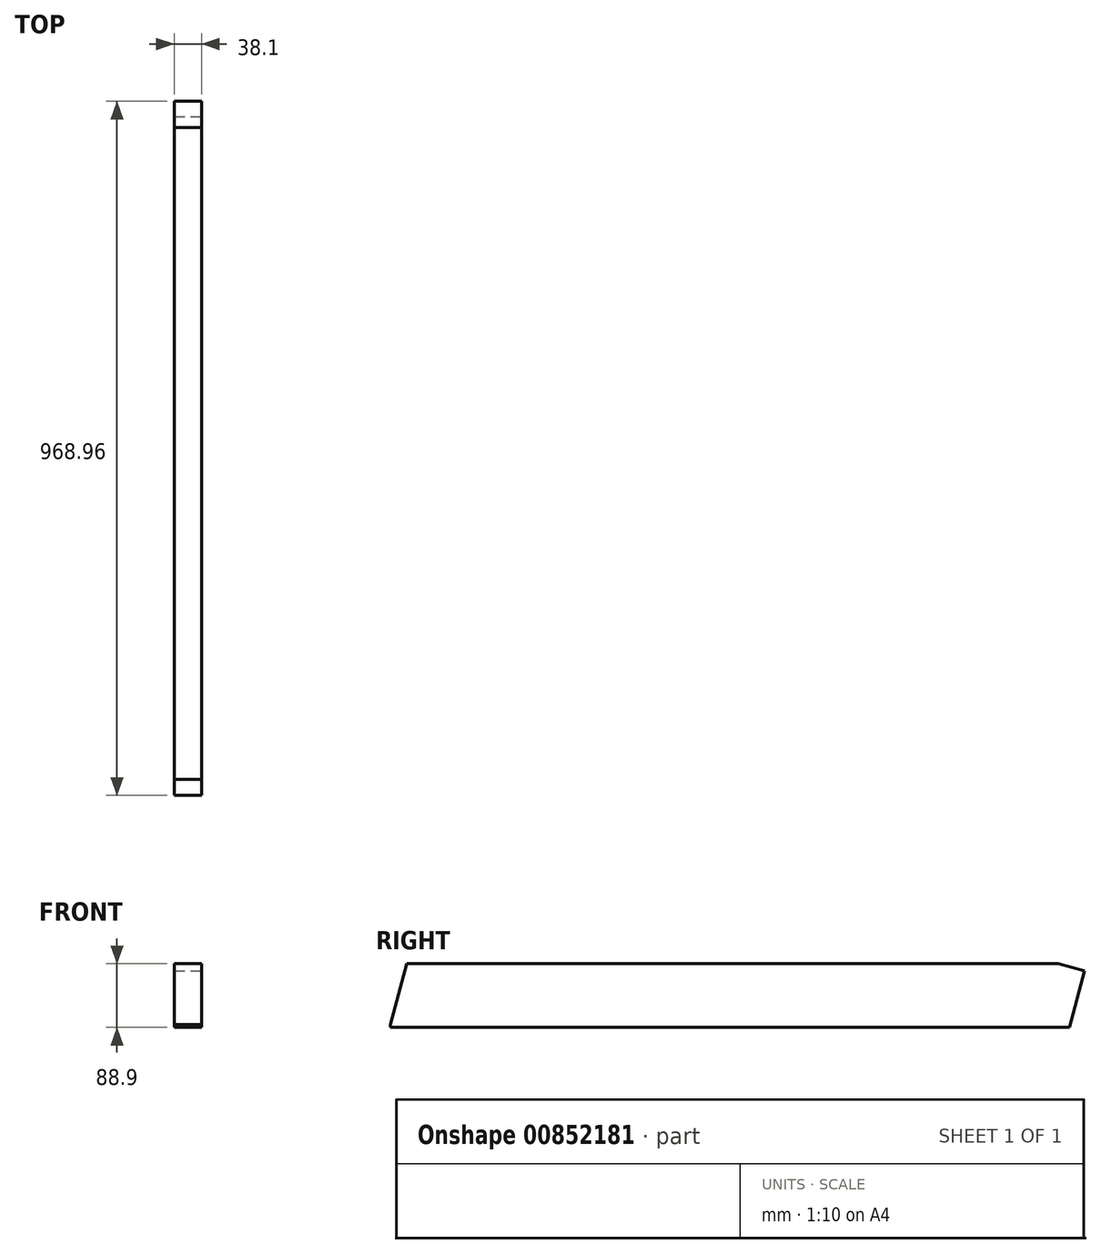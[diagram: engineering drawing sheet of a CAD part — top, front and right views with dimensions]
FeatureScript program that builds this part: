
annotation { "Feature Type Name" : "Feature", "Feature Type Description" : "" }
export const myFeature = defineFeature(function(context is Context, id is Id, definition is map)
    precondition{}
    {
        {
            var Q0;
            Q0=qCreatedBy(makeId("Front.planeOp"),FACE);
            var sketch = newSketch(context, id + "F0", { "sketchPlane" : qUnion([Q0])});
            skLineSegment(sketch, "E0.bottom", {"start": v(19.05, -44.45) * mm, "end": v(-19.05, -44.45) * mm});
            skLineSegment(sketch, "E0.top", {"start": v(19.05, 44.45) * mm, "end": v(-19.05, 44.45) * mm});
            skLineSegment(sketch, "E0.left", {"start": v(19.05, -44.45) * mm, "end": v(19.05, 44.45) * mm});
            skLineSegment(sketch, "E0.right", {"start": v(-19.05, -44.45) * mm, "end": v(-19.05, 44.45) * mm});
            skPoint(sketch, "E0.middle", {"position": v(0, 0) * mm});
            skSolve(sketch);
        }
        {
            var Q0;
            Q0=makeQuery(id+"F0.imprint","IMPRINT",FACE,{"disambiguationData":[TD([[makeQuery(id+"F0.imprint","IMPRINT",EDGE,{"derivedFrom":sQuery(id+"F0.wireOp",EDGE,"E0.bottom")}),-1.0]])]});
            extrude(context, id + "F1", {"entities" : qUnion([Q0]), "depth" : 971.65 * mm, "offsetDistance" : 25.4 * mm});
        }
        {
            var Q0;
            Q0=qCreatedBy(makeId("Right.planeOp"),FACE);
            var sketch = newSketch(context, id + "F2", { "sketchPlane" : qUnion([Q0])});
            skLineSegment(sketch, "E1", {"start": v(-948.94, 44.45) * mm, "end": v(-972.82, 44.45) * mm});
            skLineSegment(sketch, "E2", {"start": v(-972.82, 44.45) * mm, "end": v(-972.82, -44.45) * mm});
            skLineSegment(sketch, "E3", {"start": v(-972.82, -44.45) * mm, "end": v(-948.94, 44.45) * mm});
            skSolve(sketch);
        }
        {
            var Q0;
            Q0=qSketchRegion(id+"F2",true);
            extrude(context, id + "F3", {"entities" : qUnion([Q0]), "operationType" : NewBodyOperationType.REMOVE, "endBound" : BoundingType.SYMMETRIC, "oppositeDirection" : true, "depth" : 50.8 * mm, "offsetDistance" : 25.4 * mm});
        }
        {
            var Q0;
            Q0=qCreatedBy(makeId("Right.planeOp"),FACE);
            var sketch = newSketch(context, id + "F4", { "sketchPlane" : qUnion([Q0])});
            skLineSegment(sketch, "E4", {"start": v(0, -44.45) * mm, "end": v(0, 44.45) * mm});
            skLineSegment(sketch, "E5", {"start": v(0, 44.45) * mm, "end": v(-39.37, 44.45) * mm});
            skLineSegment(sketch, "E6", {"start": v(-39.37, 44.45) * mm, "end": v(-2.69, 34.62) * mm});
            skLineSegment(sketch, "E7", {"start": v(-2.69, 34.62) * mm, "end": v(-23.88, -44.45) * mm});
            skLineSegment(sketch, "E8", {"start": v(-23.88, -44.45) * mm, "end": v(0, -44.45) * mm});
            skSolve(sketch);
        }
        {
            var Q0;
            Q0=qSketchRegion(id+"F4",true);
            extrude(context, id + "F5", {"entities" : qUnion([Q0]), "operationType" : NewBodyOperationType.REMOVE, "endBound" : BoundingType.SYMMETRIC, "oppositeDirection" : true, "depth" : 50.8 * mm, "offsetDistance" : 25.4 * mm});
        }
    });
